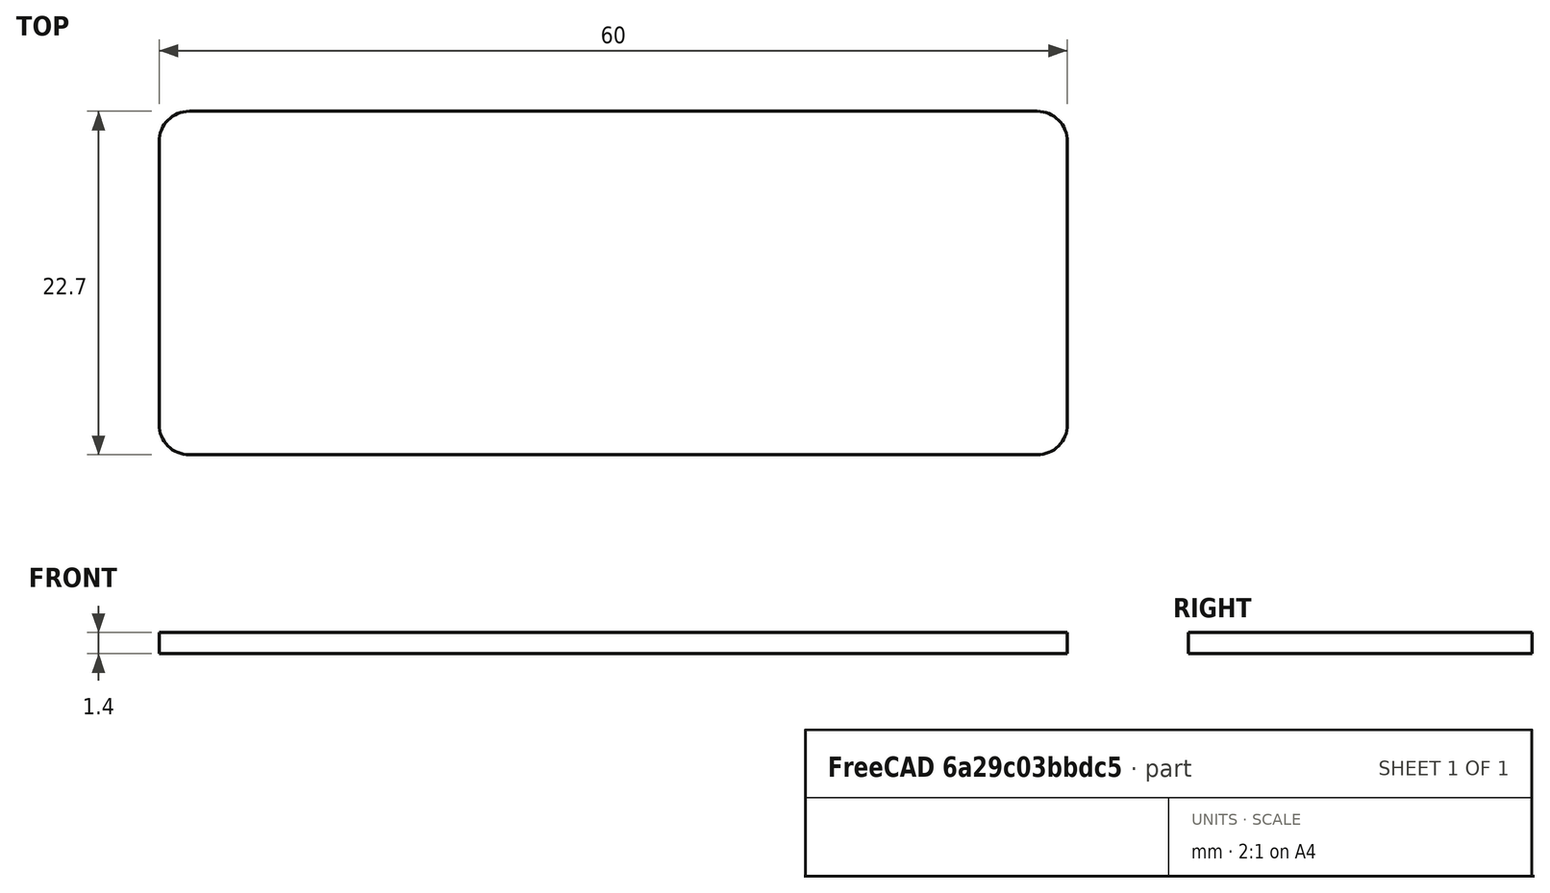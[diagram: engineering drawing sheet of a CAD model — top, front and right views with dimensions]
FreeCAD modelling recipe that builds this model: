
FCSTD DOCUMENT  (FreeCAD 1.0R39109 (Git))
Label: H1593K_coverplate
License: All rights reserved
LicenseURL: https://en.wikipedia.org/wiki/All_rights_reserved
objects: Spreadsheet::Sheet×1, Sketcher::SketchObject×1, PartDesign::Pad×1, PartDesign::Body×1
note: 6 computed .brp shape members not serialized (recipe doc carries the construction recipe); baked Part::Feature solids carry a one-line shape summary decoded from their .brp

FEATURE [Spreadsheet::Sheet] Spreadsheet
  cells = A1='Plate thickness; B1(PlateThick)=1.4; A2='Plate width; B2(PlateWidth)=60; A3='Plate height; B3(PlateHeight)=22.7; A4='Plate fillet; B4(PlateFillet)=2
FEATURE [Sketcher::SketchObject] Sketch
  ArcFitTolerance = 1e-06
  AttachmentSupport = -> [XY_Plane]
  FullyConstrained = true
  MakeInternals = false
  MapMode = 5
  expr: Constraints[23] = Spreadsheet.PlateFillet
  expr: Constraints[5] = Spreadsheet.PlateWidth
  expr: Constraints[6] = Spreadsheet.PlateHeight
  sketch-geometry (12):
    g0: LineSegment StartX=-30 StartY=9.35 StartZ=0 EndX=-30 EndY=-9.35 EndZ=0
    g1: LineSegment StartX=-28 StartY=-11.35 StartZ=0 EndX=28 EndY=-11.35 EndZ=0
    g2: LineSegment StartX=30 StartY=-9.35 StartZ=0 EndX=30 EndY=9.35 EndZ=0
    g3: LineSegment StartX=28 StartY=11.35 StartZ=0 EndX=-28 EndY=11.35 EndZ=0
    g4: ArcOfCircle CenterX=-28 CenterY=-9.35 CenterZ=0 NormalX=0 NormalY=0 NormalZ=1 AngleXU=0 Radius=2 StartAngle=3.14159 EndAngle=4.71239
    g5: GeomPoint [constr] X=-30 Y=-11.35 Z=0
    g6: ArcOfCircle CenterX=-28 CenterY=9.35 CenterZ=0 NormalX=0 NormalY=0 NormalZ=1 AngleXU=0 Radius=2 StartAngle=1.5708 EndAngle=3.14159
    g7: GeomPoint [constr] X=-30 Y=11.35 Z=0
    g8: ArcOfCircle CenterX=28 CenterY=9.35 CenterZ=0 NormalX=0 NormalY=0 NormalZ=1 AngleXU=0 Radius=2 StartAngle=3.1e-15 EndAngle=1.5708
    g9: GeomPoint [constr] X=30 Y=11.35 Z=0
    g10: ArcOfCircle CenterX=28 CenterY=-9.35 CenterZ=0 NormalX=0 NormalY=0 NormalZ=1 AngleXU=0 Radius=2 StartAngle=4.71239 EndAngle=6.28319
    g11: GeomPoint [constr] X=30 Y=-11.35 Z=0
  constraints (27):
    c: Vertical(g0)
    c: Vertical(g2)
    c: Horizontal(g1)
    c: Horizontal(g3)
    c: Symmetric(g9,g5,g-1)
    c: DistanceX(g5,g11) = 60
    c: DistanceY(g11,g9) = 22.7
    c: PointOnObject(g5,g1)
    c: PointOnObject(g5,g0)
    c: Tangent(g1,g4) = -1.5708
    c: Tangent(g0,g4) = -1.5708
    c: PointOnObject(g7,g3)
    c: PointOnObject(g7,g0)
    c: Tangent(g3,g6) = -1.5708
    c: Tangent(g0,g6) = -1.5708
    c: PointOnObject(g9,g2)
    c: PointOnObject(g9,g3)
    c: Tangent(g2,g8) = -1.5708
    c: Tangent(g3,g8) = -1.5708
    c: PointOnObject(g11,g2)
    c: PointOnObject(g11,g1)
    c: Tangent(g2,g10) = -1.5708
    c: Tangent(g1,g10) = -1.5708
    c: DistanceY(g1,g4) = 2
    c: Equal(g4,g6)
    c: Equal(g4,g8)
    c: Equal(g4,g10)
FEATURE [PartDesign::Pad] Pad  label="plate"
  Direction = (0,0,1)
  Length = 1.4
  Length2 = 10
  Profile = -> Sketch
  ReferenceAxis = -> Sketch [N_Axis]
  Refine = true
  Suppressed = false
  Type = 0
  expr: Length = Spreadsheet.PlateThick
FEATURE [PartDesign::Body] Body  label="coverplate"
  AllowCompound = false
  Group = -> [Sketch,Pad]
  Origin = -> Origin
  Tip = -> Pad
